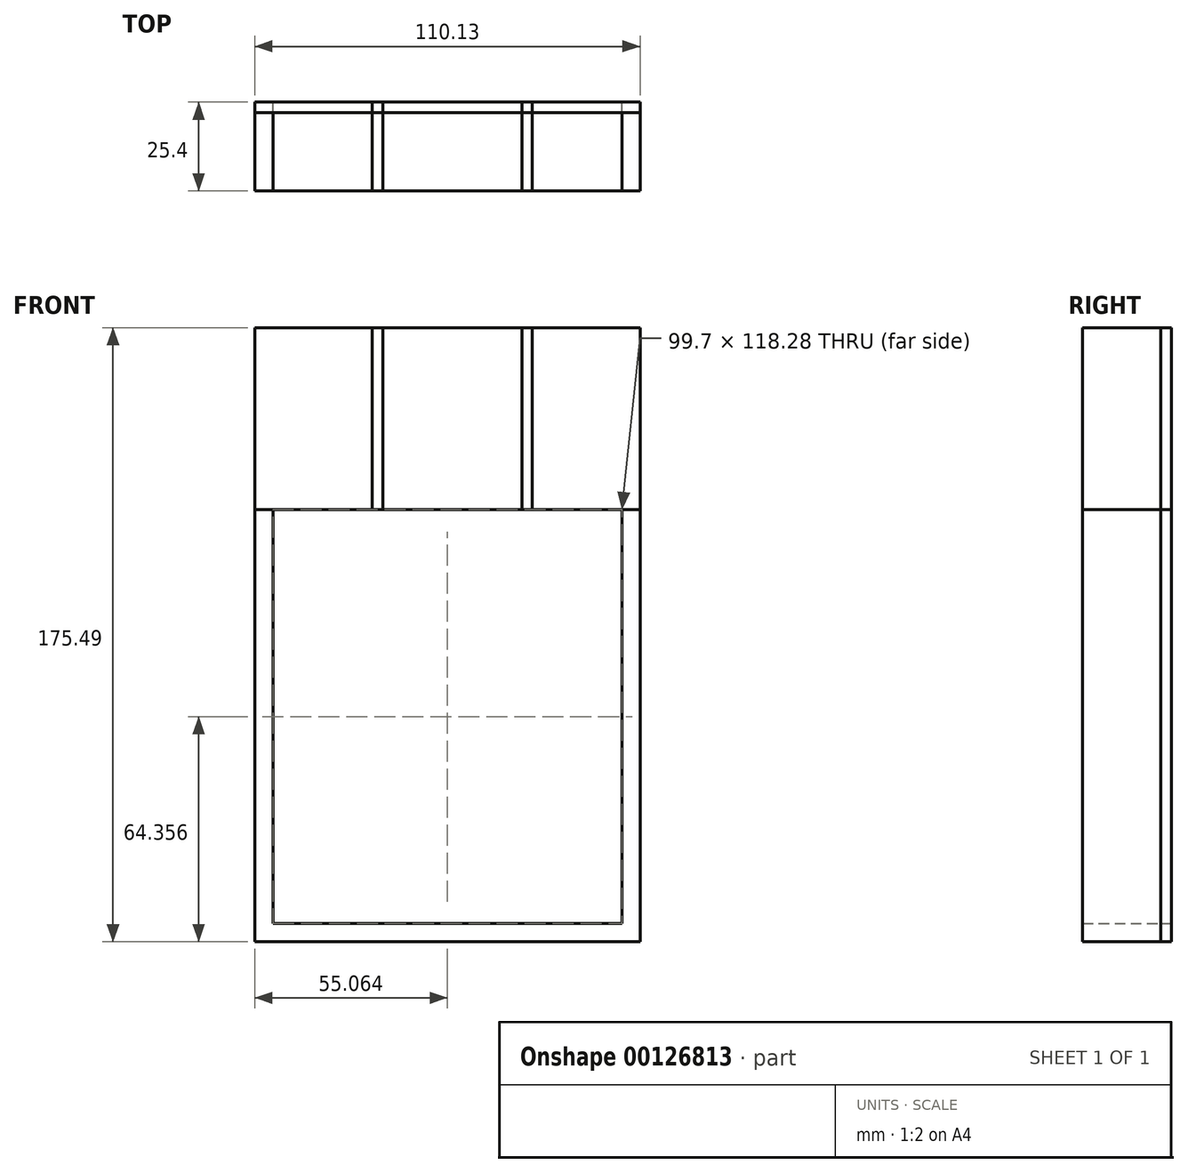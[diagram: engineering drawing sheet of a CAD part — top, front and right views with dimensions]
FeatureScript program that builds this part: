
annotation { "Feature Type Name" : "Feature", "Feature Type Description" : "" }
export const myFeature = defineFeature(function(context is Context, id is Id, definition is map)
    precondition{}
    {
        {
            var Q0;
            Q0=qCreatedBy(makeId("Front.planeOp"),FACE);
            var sketch = newSketch(context, id + "F0", { "sketchPlane" : qUnion([Q0])});
            skLineSegment(sketch, "E0.bottom", {"start": v(-113.43, 107.7) * mm, "end": v(-3.3, 107.7) * mm});
            skLineSegment(sketch, "E0.top", {"start": v(-113.43, -67.78) * mm, "end": v(-3.3, -67.78) * mm});
            skLineSegment(sketch, "E0.left", {"start": v(-113.43, 107.7) * mm, "end": v(-113.43, -67.78) * mm});
            skLineSegment(sketch, "E0.right", {"start": v(-3.3, 107.7) * mm, "end": v(-3.3, -67.78) * mm});
            skLineSegment(sketch, "E1", {"start": v(-108.22, -62.56) * mm, "end": v(-8.52, -62.56) * mm});
            skLineSegment(sketch, "E2", {"start": v(-3.3, 55.72) * mm, "end": v(-113.43, 55.72) * mm});
            skLineSegment(sketch, "E3", {"start": v(-108.22, -62.56) * mm, "end": v(-108.22, 55.72) * mm});
            skLineSegment(sketch, "E4", {"start": v(-8.52, -62.56) * mm, "end": v(-8.52, 55.72) * mm});
            skPoint(sketch, "E5", {"position": v(-79.8, 107.7) * mm});
            skPoint(sketch, "E6", {"position": v(-34.09, 107.7) * mm});
            skLineSegment(sketch, "E7", {"start": v(-79.8, 107.7) * mm, "end": v(-79.8, 55.72) * mm});
            skLineSegment(sketch, "E8", {"start": v(-34.09, 107.7) * mm, "end": v(-34.09, 55.72) * mm});
            skLineSegment(sketch, "E9", {"start": v(-76.8, 107.7) * mm, "end": v(-76.8, 55.72) * mm});
            skLineSegment(sketch, "E10", {"start": v(-37.09, 107.7) * mm, "end": v(-37.09, 55.72) * mm});
            skSolve(sketch);
        }
        {
            var Q0;
            {var subQ0=sQuery(id+"F0.wireOp",EDGE,"E7");Q0=makeQuery(id+"F0.imprint","IMPRINT",FACE,{"disambiguationData":[TD([[makeQuery(id+"F0.imprint","IMPRINT",EDGE,{"derivedFrom":subQ0}),1.0]])]});}
            var Q1;
            {var subQ0=sQuery(id+"F0.wireOp",EDGE,"E8");Q1=makeQuery(id+"F0.imprint","IMPRINT",FACE,{"disambiguationData":[TD([[makeQuery(id+"F0.imprint","IMPRINT",EDGE,{"derivedFrom":subQ0}),-1.0]])]});}
            var Q2;
            {var subQ1=sQuery(id+"F0.wireOp",EDGE,"E0.top");Q2=makeQuery(id+"F0.imprint","IMPRINT",FACE,{"disambiguationData":[TD([[makeQuery(id+"F0.imprint","IMPRINT",EDGE,{"derivedFrom":subQ1}),1.0]])]});}
            extrude(context, id + "F1", {"entities" : qUnion([Q0, Q1, Q2]), "depth" : 25.4 * mm});
        }
        {
            var Q0;
            Q0 = qSketchRegion(id + "F0", true);
            extrude(context, id + "F2", {"entities" : qUnion([Q0]), "depth" : 3 * mm});
        }
        {
            var Q0;
            Q0=makeQuery(id+"F0.imprint","IMPRINT",FACE,{"disambiguationData":[TD([[makeQuery(id+"F0.imprint","IMPRINT",EDGE,{"derivedFrom":sQuery(id+"F0.wireOp",EDGE,"E1")}),1.0]])]});
            extrude(context, id + "F3", {"entities" : qUnion([Q0]), "depth" : 3 * mm});
        }
    });
